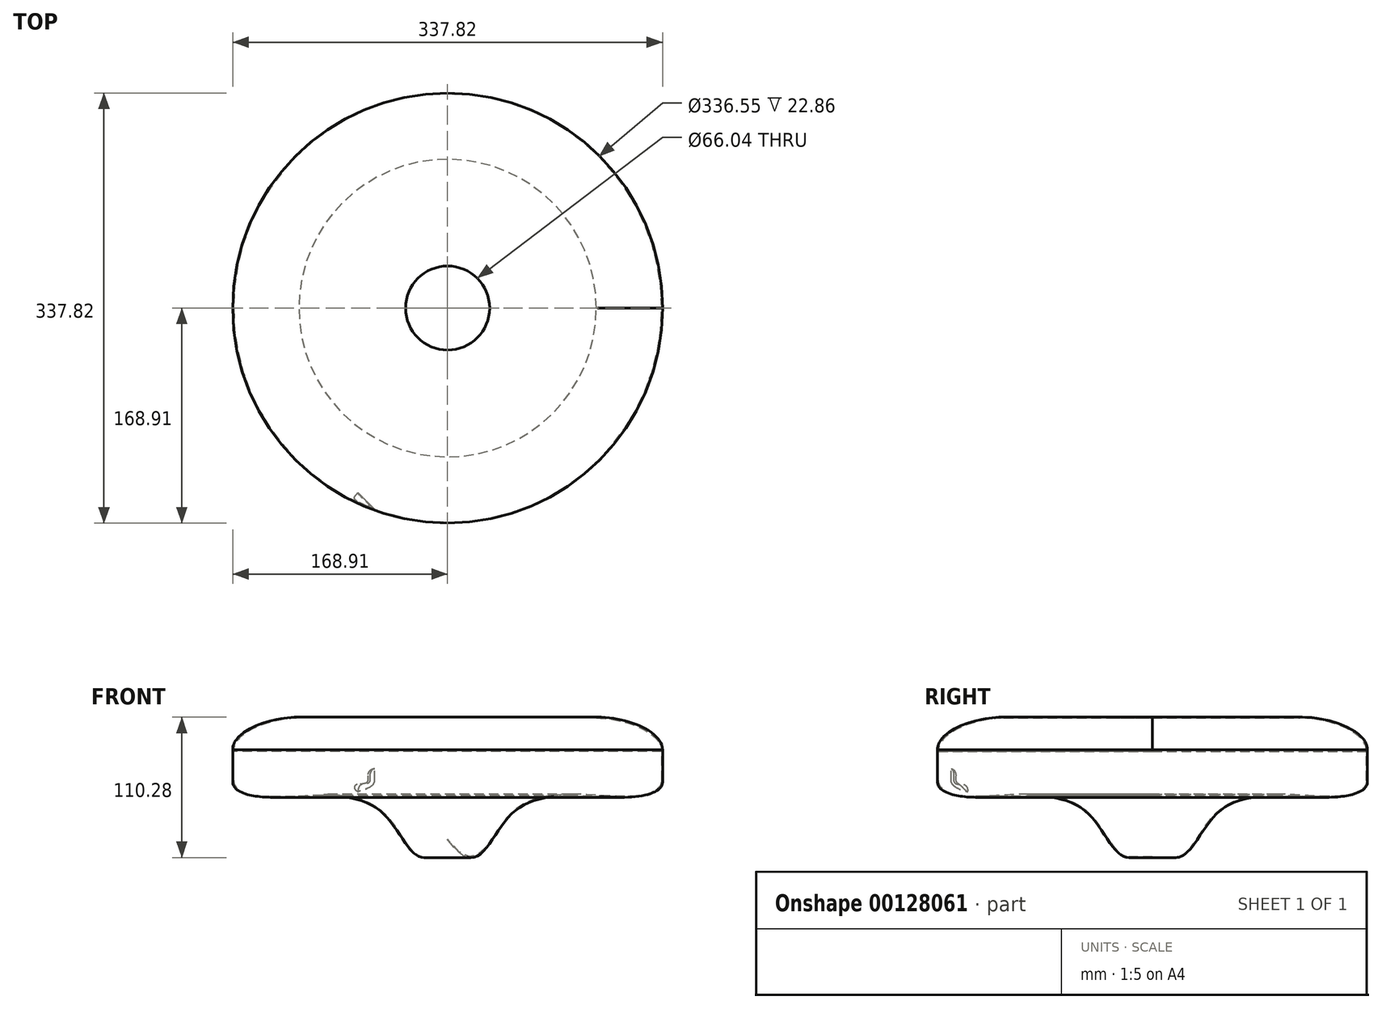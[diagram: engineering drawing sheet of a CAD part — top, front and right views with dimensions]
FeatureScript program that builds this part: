
annotation { "Feature Type Name" : "Feature", "Feature Type Description" : "" }
export const myFeature = defineFeature(function(context is Context, id is Id, definition is map)
    precondition{}
    {
        {
            var Q0;
            Q0=qCreatedBy(makeId("Front.planeOp"),FACE);
            var sketch = newSketch(context, id + "F0", { "sketchPlane" : qUnion([Q0])});
            skLineSegment(sketch, "E0", {"start": v(168.28, -25.58) * mm, "end": v(168.28, -48.44) * mm});
            skLineSegment(sketch, "E1", {"start": v(116.85, 0.52) * mm, "end": v(33.02, 0.52) * mm});
            skLineSegment(sketch, "E2", {"start": v(33.02, 0.52) * mm, "end": v(33.02, 1.16) * mm});
            skLineSegment(sketch, "E3", {"start": v(33.02, 1.16) * mm, "end": v(117.88, 1.16) * mm});
            skLineSegment(sketch, "E4", {"start": v(168.91, -49.91) * mm, "end": v(168.91, -24.51) * mm});
            skLineSegment(sketch, "E5", {"start": v(0, -95.36) * mm, "end": v(0, -94.73) * mm});
            skLineSegment(sketch, "E6", {"start": v(0, 0) * mm, "end": v(0, -95.36) * mm, "construction": true});
            skFitSpline(sketch, "E7", {"points": [v(0, -95.36) * mm, v(49.62, -75.5) * mm, v(141.06, -61.74) * mm, v(168.91, -49.91) * mm], "startDerivative": vector(232.63, -308.48) * mm, "endDerivative": vector(0.88, 88.95) * mm});
            skFitSpline(sketch, "E8", {"points": [v(168.28, -48.44) * mm, v(141.06, -61.12) * mm, v(49.62, -74.42) * mm, v(0, -94.73) * mm], "startDerivative": vector(-1.03, -105.83) * mm, "endDerivative": vector(-232.12, 309.4) * mm});
            skFitSpline(sketch, "E9", {"points": [v(116.85, 0.52) * mm, v(168.28, -25.58) * mm], "startDerivative": vector(72.47, -1.57) * mm, "endDerivative": vector(0, -44.09) * mm});
            skFitSpline(sketch, "E10", {"points": [v(168.91, -24.51) * mm, v(117.88, 1.16) * mm], "startDerivative": vector(0, 44.26) * mm, "endDerivative": vector(-69.05, 0) * mm});
            skSolve(sketch);
        }
        {
            var Q0;
            Q0=makeQuery(id+"F0.imprint","IMPRINT",FACE,{"disambiguationData":[TD([[makeQuery(id+"F0.imprint","IMPRINT",EDGE,{"derivedFrom":sQuery(id+"F0.wireOp",EDGE,"E0")}),1.0]])]});
            var Q1;
            Q1=sQuery(id+"F0.wireOp",EDGE,"E6");
            revolve(context, id + "F1", {"entities" : qUnion([Q0]), "axis" : qUnion([Q1]), "revolveType" : RevolveType.FULL});
        }
        {
            var Q0;
            Q0=qCreatedBy(makeId("Front.planeOp"),FACE);
            var Q1;
            Q1=qCreatedBy(makeId("Right.planeOp"),FACE);
            cPlane(context, id + "F2", {"entities" : qUnion([Q0, Q1]), "cplaneType" : CPlaneType.MID_PLANE, "offset" : 25.4 * mm, "width" : 152.4 * mm, "height" : 152.4 * mm});
        }
        {
            var Q0;
            Q0=qCreatedBy(id+"F2.planeOp",FACE);
            cPlane(context, id + "F3", {"entities" : qUnion([Q0]), "cplaneType" : CPlaneType.OFFSET, "offset" : 152.4 * mm, "width" : 152.4 * mm, "height" : 152.4 * mm});
        }
        {
            var Q0;
            Q0=qCreatedBy(id+"F3.planeOp",FACE);
            var sketch = newSketch(context, id + "F4", { "sketchPlane" : qUnion([Q0])});
            skFitSpline(sketch, "E11", {"points": [v(71.8, -39.5) * mm, v(70.5, -51.03) * mm, v(52.85, -57.4) * mm], "startDerivative": vector(-1.65, -55.88) * mm, "endDerivative": vector(-57, -10.9) * mm});
            skLineSegment(sketch, "E12", {"start": v(71.8, -39.5) * mm, "end": v(71.14, -39.5) * mm});
            skLineSegment(sketch, "E13", {"start": v(52.85, -57.4) * mm, "end": v(52.85, -56.73) * mm});
            skFitSpline(sketch, "E14", {"points": [v(67.6, -39.5) * mm, v(65.71, -49.53) * mm, v(52.85, -52.8) * mm], "startDerivative": vector(-19.73, -15.25) * mm, "endDerivative": vector(-23.87, -11.23) * mm});
            skArc(sketch, "E15.filletArc", {"start": v(57.32, -51.69) * mm, "mid": v(54.13, -53.36) * mm, "end": v(52.85, -56.73) * mm});
            skArc(sketch, "E16.filletArc", {"start": v(71.14, -39.5) * mm, "mid": v(67.44, -41.1) * mm, "end": v(66.07, -44.88) * mm});
            skSolve(sketch);
        }
        {
            var Q0;
            Q0=makeQuery(id+"F4.imprint","IMPRINT",FACE,{"disambiguationData":[TD([[makeQuery(id+"F4.imprint","IMPRINT",EDGE,{"derivedFrom":sQuery(id+"F4.wireOp",EDGE,"E11")}),-1.0]])]});
            extrude(context, id + "F5", {"entities" : qUnion([Q0]), "operationType" : NewBodyOperationType.ADD, "endBound" : BoundingType.UP_TO_NEXT, "depth" : 0.25 * mm});
        }
    });
